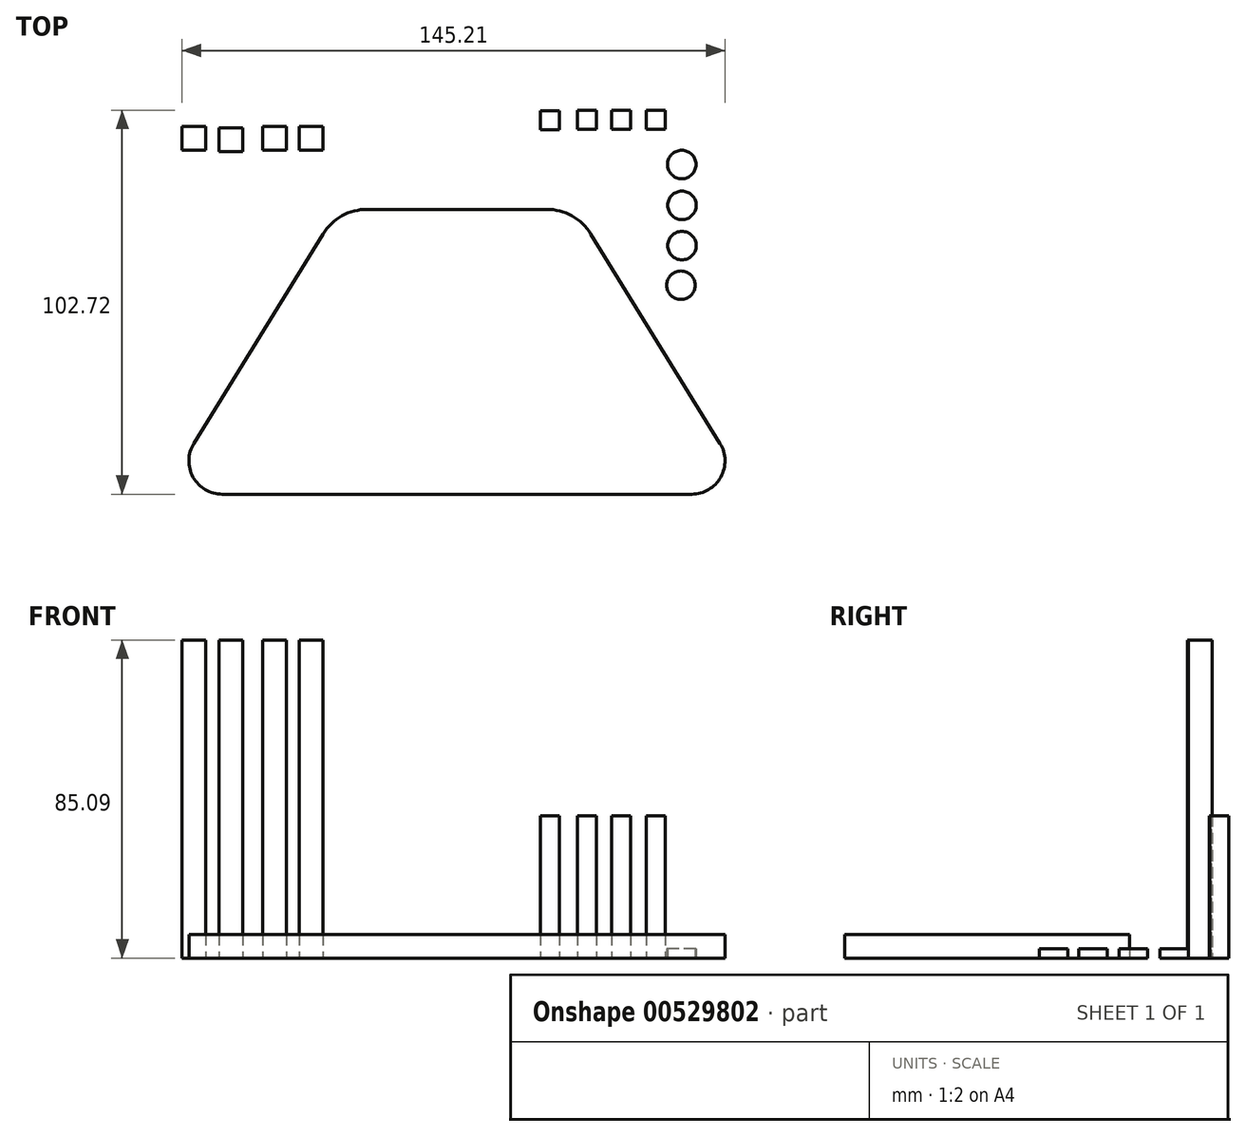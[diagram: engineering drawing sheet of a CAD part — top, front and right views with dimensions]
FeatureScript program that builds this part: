
annotation { "Feature Type Name" : "Feature", "Feature Type Description" : "" }
export const myFeature = defineFeature(function(context is Context, id is Id, definition is map)
    precondition{}
    {
        {
            var Q0;
            Q0=qCreatedBy(makeId("Top.planeOp"),FACE);
            var sketch = newSketch(context, id + "F0", { "sketchPlane" : qUnion([Q0])});
            skLineSegment(sketch, "E0.bottom", {"start": v(-23.95, 38.1) * mm, "end": v(23.95, 38.1) * mm});
            skLineSegment(sketch, "E0.top", {"start": v(-31.75, -38.1) * mm, "end": v(31.75, -38.1) * mm});
            skLineSegment(sketch, "E0.left", {"start": v(-31.75, 38.1) * mm, "end": v(-31.75, -38.1) * mm});
            skLineSegment(sketch, "E0.right", {"start": v(31.75, 38.1) * mm, "end": v(31.75, -38.1) * mm});
            skPoint(sketch, "E0.middle", {"position": v(0, 0) * mm});
            skLineSegment(sketch, "E1", {"start": v(-31.75, -38.1) * mm, "end": v(-62.81, -38.1) * mm});
            skLineSegment(sketch, "E2", {"start": v(31.75, -38.1) * mm, "end": v(62.81, -38.1) * mm});
            skLineSegment(sketch, "E3", {"start": v(-70.38, -24.54) * mm, "end": v(-35.84, 31.46) * mm});
            skLineSegment(sketch, "E4", {"start": v(35.84, 31.46) * mm, "end": v(70.38, -24.54) * mm});
            skPoint(sketch, "E5.visualSharp", {"position": v(-31.75, 38.1) * mm});
            skArc(sketch, "E5.filletArc", {"start": v(-23.95, 38.1) * mm, "mid": v(-30.76, 36.33) * mm, "end": v(-35.84, 31.46) * mm});
            skPoint(sketch, "E6.visualSharp", {"position": v(31.75, 38.1) * mm});
            skArc(sketch, "E6.filletArc", {"start": v(35.84, 31.46) * mm, "mid": v(30.76, 36.33) * mm, "end": v(23.95, 38.1) * mm});
            skPoint(sketch, "E7.visualSharp", {"position": v(-78.74, -38.1) * mm});
            skArc(sketch, "E7.filletArc", {"start": v(-70.38, -24.54) * mm, "mid": v(-70.58, -33.54) * mm, "end": v(-62.81, -38.1) * mm});
            skPoint(sketch, "E8.visualSharp", {"position": v(78.74, -38.1) * mm});
            skArc(sketch, "E8.filletArc", {"start": v(62.81, -38.1) * mm, "mid": v(70.58, -33.54) * mm, "end": v(70.38, -24.54) * mm});
            skSolve(sketch);
        }
        {
            var Q0;
            {var subQ4=sQuery(id+"F0.wireOp",EDGE,"E1");Q0=makeQuery(id+"F0.imprint","IMPRINT",FACE,{"disambiguationData":[TD([[makeQuery(id+"F0.imprint","IMPRINT",EDGE,{"derivedFrom":subQ4}),-1.0]])]});}
            var Q1;
            {var subQ7=sQuery(id+"F0.wireOp",EDGE,"E0.bottom");Q1=makeQuery(id+"F0.imprint","IMPRINT",FACE,{"disambiguationData":[TD([[makeQuery(id+"F0.imprint","IMPRINT",EDGE,{"derivedFrom":subQ7}),-1.0]])]});}
            var Q2;
            {var subQ4=sQuery(id+"F0.wireOp",EDGE,"E2");Q2=makeQuery(id+"F0.imprint","IMPRINT",FACE,{"disambiguationData":[TD([[makeQuery(id+"F0.imprint","IMPRINT",EDGE,{"derivedFrom":subQ4}),1.0]])]});}
            extrude(context, id + "F1", {"entities" : qUnion([Q0, Q1, Q2]), "depth" : 6.35 * mm, "offsetDistance" : 25.4 * mm});
        }
        {
            var Q0;
            Q0=qCreatedBy(makeId("Top.planeOp"),FACE);
            var sketch = newSketch(context, id + "F2", { "sketchPlane" : qUnion([Q0])});
            skLineSegment(sketch, "E9.bottom", {"start": v(-63.68, 59.93) * mm, "end": v(-57.33, 59.93) * mm});
            skLineSegment(sketch, "E9.top", {"start": v(-63.68, 53.58) * mm, "end": v(-57.33, 53.58) * mm});
            skLineSegment(sketch, "E9.left", {"start": v(-63.68, 59.93) * mm, "end": v(-63.68, 53.58) * mm});
            skLineSegment(sketch, "E9.right", {"start": v(-57.33, 59.93) * mm, "end": v(-57.33, 53.58) * mm});
            skPoint(sketch, "E9.middle", {"position": v(-60.5, 56.75) * mm});
            skPoint(sketch, "E10.cornerSnap0", {"position": v(-60.5, 59.93) * mm});
            skLineSegment(sketch, "E11.bottom", {"start": v(-73.51, 60.23) * mm, "end": v(-67.16, 60.23) * mm});
            skLineSegment(sketch, "E11.top", {"start": v(-73.51, 53.88) * mm, "end": v(-67.16, 53.88) * mm});
            skLineSegment(sketch, "E11.left", {"start": v(-73.51, 60.23) * mm, "end": v(-73.51, 53.88) * mm});
            skLineSegment(sketch, "E11.right", {"start": v(-67.16, 60.23) * mm, "end": v(-67.16, 53.88) * mm});
            skPoint(sketch, "E11.middle", {"position": v(-70.34, 57.06) * mm});
            skPoint(sketch, "E12.cornerSnap0", {"position": v(-70.34, 60.23) * mm});
            skLineSegment(sketch, "E13.bottom", {"start": v(-52.01, 60.23) * mm, "end": v(-45.66, 60.23) * mm});
            skLineSegment(sketch, "E13.top", {"start": v(-52.01, 53.88) * mm, "end": v(-45.66, 53.88) * mm});
            skLineSegment(sketch, "E13.left", {"start": v(-52.01, 60.23) * mm, "end": v(-52.01, 53.88) * mm});
            skLineSegment(sketch, "E13.right", {"start": v(-45.66, 60.23) * mm, "end": v(-45.66, 53.88) * mm});
            skPoint(sketch, "E13.middle", {"position": v(-48.84, 57.06) * mm});
            skPoint(sketch, "E14.cornerSnap0", {"position": v(-48.84, 60.23) * mm});
            skLineSegment(sketch, "E15.bottom", {"start": v(-42.18, 60.23) * mm, "end": v(-35.83, 60.23) * mm});
            skLineSegment(sketch, "E15.top", {"start": v(-42.18, 53.88) * mm, "end": v(-35.83, 53.88) * mm});
            skLineSegment(sketch, "E15.left", {"start": v(-42.18, 60.23) * mm, "end": v(-42.18, 53.88) * mm});
            skLineSegment(sketch, "E15.right", {"start": v(-35.83, 60.23) * mm, "end": v(-35.83, 53.88) * mm});
            skPoint(sketch, "E15.middle", {"position": v(-39, 57.06) * mm});
            skPoint(sketch, "E16.cornerSnap0", {"position": v(-39, 60.23) * mm});
            skSolve(sketch);
        }
        {
            var Q0;
            Q0=makeQuery(id+"F2.imprint","IMPRINT",FACE,{"disambiguationData":[TD([[makeQuery(id+"F2.imprint","IMPRINT",EDGE,{"derivedFrom":sQuery(id+"F2.wireOp",EDGE,"E9.bottom")}),-1.0]])]});
            var Q1;
            Q1=makeQuery(id+"F2.imprint","IMPRINT",FACE,{"disambiguationData":[TD([[makeQuery(id+"F2.imprint","IMPRINT",EDGE,{"derivedFrom":sQuery(id+"F2.wireOp",EDGE,"E11.bottom")}),-1.0]])]});
            var Q2;
            Q2=makeQuery(id+"F2.imprint","IMPRINT",FACE,{"disambiguationData":[TD([[makeQuery(id+"F2.imprint","IMPRINT",EDGE,{"derivedFrom":sQuery(id+"F2.wireOp",EDGE,"E13.bottom")}),-1.0]])]});
            var Q3;
            Q3=makeQuery(id+"F2.imprint","IMPRINT",FACE,{"disambiguationData":[TD([[makeQuery(id+"F2.imprint","IMPRINT",EDGE,{"derivedFrom":sQuery(id+"F2.wireOp",EDGE,"E15.bottom")}),-1.0]])]});
            extrude(context, id + "F3", {"entities" : qUnion([Q0, Q1, Q2, Q3]), "depth" : 85.1 * mm, "offsetDistance" : 25.4 * mm});
        }
        {
            var Q0;
            Q0=qCreatedBy(makeId("Top.planeOp"),FACE);
            var sketch = newSketch(context, id + "F4", { "sketchPlane" : qUnion([Q0])});
            skLineSegment(sketch, "E17.bottom", {"start": v(22.32, 64.5) * mm, "end": v(27.4, 64.5) * mm});
            skLineSegment(sketch, "E17.top", {"start": v(22.32, 59.41) * mm, "end": v(27.4, 59.41) * mm});
            skLineSegment(sketch, "E17.left", {"start": v(22.32, 64.5) * mm, "end": v(22.32, 59.41) * mm});
            skLineSegment(sketch, "E17.right", {"start": v(27.4, 64.5) * mm, "end": v(27.4, 59.41) * mm});
            skPoint(sketch, "E17.middle", {"position": v(24.86, 61.95) * mm});
            skPoint(sketch, "E18.cornerSnap0", {"position": v(24.86, 64.5) * mm});
            skLineSegment(sketch, "E19.bottom", {"start": v(32.17, 64.62) * mm, "end": v(37.25, 64.62) * mm});
            skLineSegment(sketch, "E19.top", {"start": v(32.17, 59.54) * mm, "end": v(37.25, 59.54) * mm});
            skLineSegment(sketch, "E19.left", {"start": v(32.17, 64.62) * mm, "end": v(32.17, 59.54) * mm});
            skLineSegment(sketch, "E19.right", {"start": v(37.25, 64.62) * mm, "end": v(37.25, 59.54) * mm});
            skPoint(sketch, "E19.middle", {"position": v(34.7, 62.08) * mm});
            skPoint(sketch, "E20.cornerSnap0", {"position": v(34.7, 64.62) * mm});
            skLineSegment(sketch, "E21.bottom", {"start": v(41.38, 64.62) * mm, "end": v(46.46, 64.62) * mm});
            skLineSegment(sketch, "E21.top", {"start": v(41.38, 59.54) * mm, "end": v(46.46, 59.54) * mm});
            skLineSegment(sketch, "E21.left", {"start": v(41.38, 64.62) * mm, "end": v(41.38, 59.54) * mm});
            skLineSegment(sketch, "E21.right", {"start": v(46.46, 64.62) * mm, "end": v(46.46, 59.54) * mm});
            skPoint(sketch, "E21.middle", {"position": v(43.92, 62.08) * mm});
            skPoint(sketch, "E22.cornerSnap0", {"position": v(43.92, 64.62) * mm});
            skLineSegment(sketch, "E23.bottom", {"start": v(50.6, 64.62) * mm, "end": v(55.68, 64.62) * mm});
            skLineSegment(sketch, "E23.top", {"start": v(50.6, 59.54) * mm, "end": v(55.68, 59.54) * mm});
            skLineSegment(sketch, "E23.left", {"start": v(50.6, 64.62) * mm, "end": v(50.6, 59.54) * mm});
            skLineSegment(sketch, "E23.right", {"start": v(55.68, 64.62) * mm, "end": v(55.68, 59.54) * mm});
            skPoint(sketch, "E23.middle", {"position": v(53.14, 62.08) * mm});
            skPoint(sketch, "E24.cornerSnap0", {"position": v(53.14, 64.62) * mm});
            skSolve(sketch);
        }
        {
            var Q0;
            Q0=makeQuery(id+"F4.imprint","IMPRINT",FACE,{"disambiguationData":[TD([[makeQuery(id+"F4.imprint","IMPRINT",EDGE,{"derivedFrom":sQuery(id+"F4.wireOp",EDGE,"E19.bottom")}),-1.0]])]});
            var Q1;
            Q1=makeQuery(id+"F4.imprint","IMPRINT",FACE,{"disambiguationData":[TD([[makeQuery(id+"F4.imprint","IMPRINT",EDGE,{"derivedFrom":sQuery(id+"F4.wireOp",EDGE,"E17.bottom")}),-1.0]])]});
            var Q2;
            Q2=makeQuery(id+"F4.imprint","IMPRINT",FACE,{"disambiguationData":[TD([[makeQuery(id+"F4.imprint","IMPRINT",EDGE,{"derivedFrom":sQuery(id+"F4.wireOp",EDGE,"E21.bottom")}),-1.0]])]});
            var Q3;
            Q3=makeQuery(id+"F4.imprint","IMPRINT",FACE,{"disambiguationData":[TD([[makeQuery(id+"F4.imprint","IMPRINT",EDGE,{"derivedFrom":sQuery(id+"F4.wireOp",EDGE,"E23.bottom")}),-1.0]])]});
            extrude(context, id + "F5", {"entities" : qUnion([Q0, Q1, Q2, Q3]), "depth" : 38.1 * mm, "offsetDistance" : 25.4 * mm});
        }
        {
            var Q0;
            Q0=qCreatedBy(makeId("Top.planeOp"),FACE);
            var sketch = newSketch(context, id + "F6", { "sketchPlane" : qUnion([Q0])});
            skCircle(sketch, "E25", {"center": v(60.13, 50.08) * mm, "radius": 3.81 * mm});
            skCircle(sketch, "E26", {"center": v(60.2, 39.16) * mm, "radius": 3.81 * mm});
            skCircle(sketch, "E27", {"center": v(59.93, 17.78) * mm, "radius": 3.81 * mm});
            skCircle(sketch, "E28", {"center": v(60.2, 28.39) * mm, "radius": 3.81 * mm});
            skSolve(sketch);
        }
        {
            var Q0;
            Q0=makeQuery(id+"F6.imprint","IMPRINT",FACE,{"disambiguationData":[TD([[makeQuery(id+"F6.imprint","IMPRINT",EDGE,{"derivedFrom":sQuery(id+"F6.wireOp",EDGE,"E25")}),1.0]])]});
            var Q1;
            Q1=makeQuery(id+"F6.imprint","IMPRINT",FACE,{"disambiguationData":[TD([[makeQuery(id+"F6.imprint","IMPRINT",EDGE,{"derivedFrom":sQuery(id+"F6.wireOp",EDGE,"E26")}),1.0]])]});
            var Q2;
            Q2=makeQuery(id+"F6.imprint","IMPRINT",FACE,{"disambiguationData":[TD([[makeQuery(id+"F6.imprint","IMPRINT",EDGE,{"derivedFrom":sQuery(id+"F6.wireOp",EDGE,"E28")}),1.0]])]});
            var Q3;
            Q3=makeQuery(id+"F6.imprint","IMPRINT",FACE,{"disambiguationData":[TD([[makeQuery(id+"F6.imprint","IMPRINT",EDGE,{"derivedFrom":sQuery(id+"F6.wireOp",EDGE,"E27")}),1.0]])]});
            extrude(context, id + "F7", {"entities" : qUnion([Q0, Q1, Q2, Q3]), "depth" : 2.54 * mm, "offsetDistance" : 25.4 * mm});
        }
    });
